# Revit family: VG_Арматура_УзелНижнегоПодключенияРадиаторов_ОдинарныйУгловой_VG-608201_VALOGIN
name_source: partatom
category: Арматура трубопроводов
units: mm (PartAtom-declared; Revit-internal decimal feet)

## family parameters
Всегда вертикально = Да
На основе рабочей плоскости = Нет
Общий = Нет
При загрузке вырезать с полостями = Нет
Размер круглого соединителя = Использовать диаметр
Тип детали = Нормальный

## types (1)
- VG_Арматура_УзелНижнегоПодключенияРадиаторов_ОдинарныйУгловой_VG-608201_VALOGIN
    ADSK_URL документации изделия = https://valogin.technology
    ADSK_URL страницы изделия = https://valogin.technology
    ADSK_Версия Revit = 2019
    ADSK_Версия семейства = v.1.0
    ADSK_Группирование = Радиаторная арматура
    ADSK_Единица измерения = шт.
    ADSK_Завод-изготовитель = VALOGIN
    ADSK_Код изделия = VG-608201
    ADSK_Количество = 1
    ADSK_Марка = VG-608201
    ADSK_Масса = 0.137
    ADSK_Масса_Текст = 0.137
    ADSK_Материал = VG_Металл_Серебро_VALOGIN
    ADSK_Наименование = Узел одинарный, угловой с вентильными затворами для подключения радиаторов в двухтрубных системах отопления
    ADSK_Наименование краткое = Узел одинарный, угловой
    ADSK_Размер_Высота = 33 мм
    ADSK_Размер_Глубина = 31 мм
    ADSK_Размер_Диаметр = 20 мм
    ADSK_Размер_Ширина = 33 мм
    BL_BIM library = https://bimlib.pro
    URL = https://valogin.technology
    Изготовитель = VALOGIN
    Максимальная рабочая температура теплоносителя = 120 °C
    Максимальный коэффициент пропускной способности = 1.9 м³/ч
    Номинальное давление = 1.0 МПа
    Описание = Назначение: Одинарные узлы арт. VG-608101 и VG-608201 применяются для подключения отопительных приборов
с нижним выходом присоединительных патрубков с соединением типа 3/4" «евроконус» или внутренней
резьбой 1/2" и с любым межосевым расстоянием патрубков. Для подключения одного радиатора необходимо два одинарных узла.
    Пробное давление = 1.5 МПа
    Размер = 3/4", «плоскость»
    Средний полный срок службы = 20 лет
